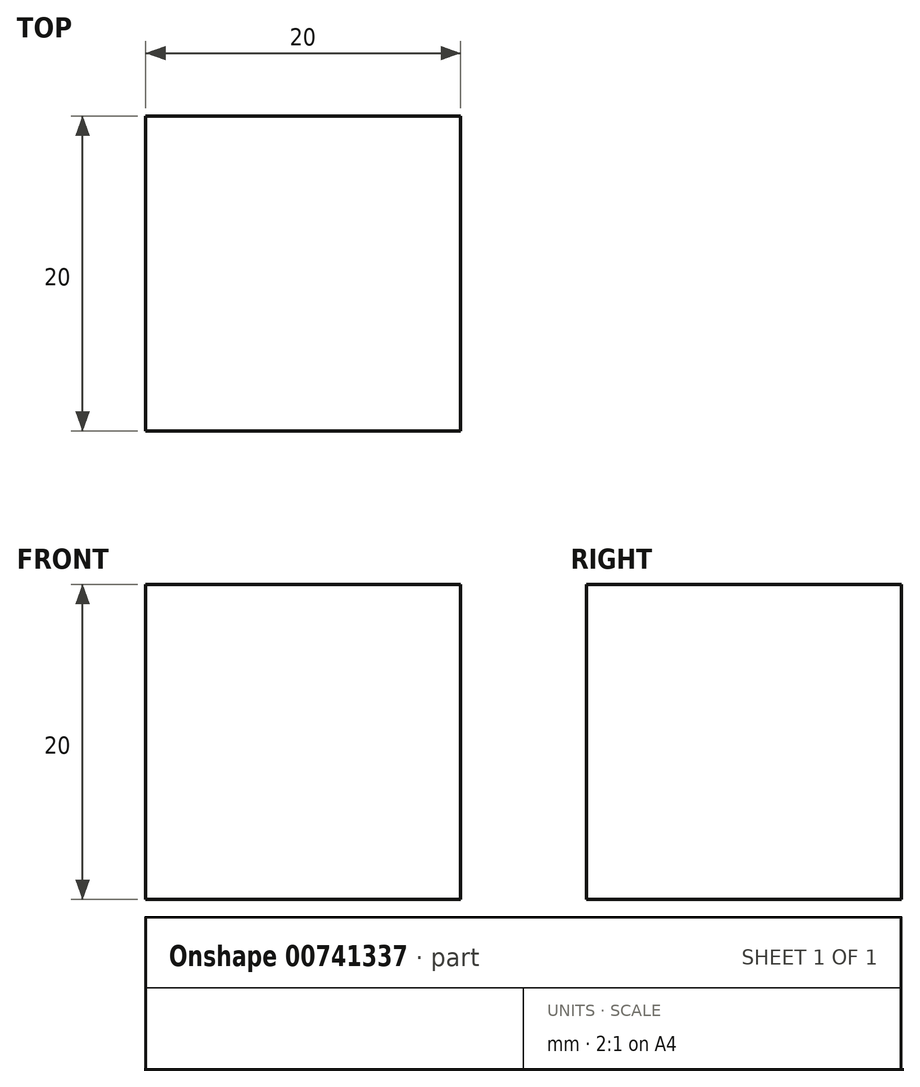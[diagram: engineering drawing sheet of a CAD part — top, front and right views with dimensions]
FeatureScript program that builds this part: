
annotation { "Feature Type Name" : "Feature", "Feature Type Description" : "" }
export const myFeature = defineFeature(function(context is Context, id is Id, definition is map)
    precondition{}
    {
        {
            var Q0;
            Q0=qCreatedBy(makeId("Top.planeOp"),FACE);
            var sketch = newSketch(context, id + "F0", { "sketchPlane" : qUnion([Q0])});
            skLineSegment(sketch, "E0", {"start": v(0, 0) * mm, "end": v(-20, 0) * mm});
            skLineSegment(sketch, "E1", {"start": v(-20, 0) * mm, "end": v(-20, 20) * mm});
            skLineSegment(sketch, "E2", {"start": v(-20, 20) * mm, "end": v(0, 0) * mm});
            skLineSegment(sketch, "E3.MirrorCS", {"start": v(0, 20) * mm, "end": v(-20, 20) * mm});
            skLineSegment(sketch, "E4.MirrorCS", {"start": v(0, 0) * mm, "end": v(0, 20) * mm});
            skSolve(sketch);
        }
        {
            var Q0;
            Q0=makeQuery(id+"F0.imprint","IMPRINT",FACE,{"disambiguationData":[TD([[makeQuery(id+"F0.imprint","IMPRINT",EDGE,{"derivedFrom":sQuery(id+"F0.wireOp",EDGE,"E0")}),-1.0]])]});
            extrude(context, id + "F1", {"entities" : qUnion([Q0]), "depth" : 20 * mm, "offsetDistance" : 25 * mm});
        }
        {
            var Q0;
            Q0=makeQuery(id+"F0.imprint","IMPRINT",FACE,{"disambiguationData":[TD([[makeQuery(id+"F0.imprint","IMPRINT",EDGE,{"derivedFrom":sQuery(id+"F0.wireOp",EDGE,"E2")}),1.0]])]});
            extrude(context, id + "F2", {"entities" : qUnion([Q0]), "operationType" : NewBodyOperationType.ADD, "depth" : 20 * mm, "offsetDistance" : 25 * mm});
        }
    });
